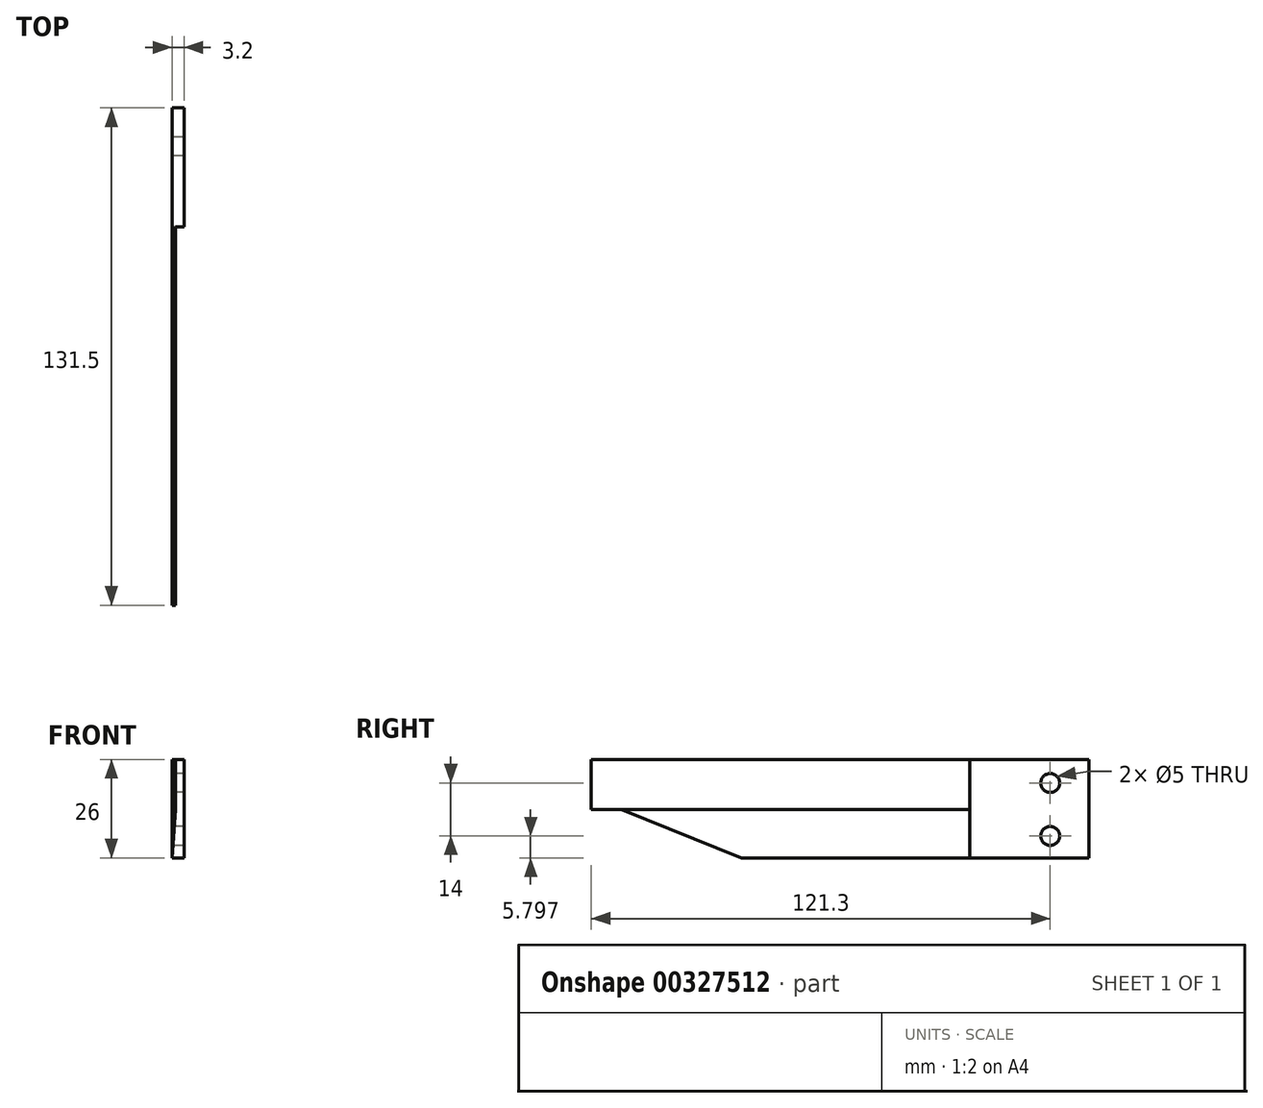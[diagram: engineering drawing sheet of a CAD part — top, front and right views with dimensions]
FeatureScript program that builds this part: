
annotation { "Feature Type Name" : "Feature", "Feature Type Description" : "" }
export const myFeature = defineFeature(function(context is Context, id is Id, definition is map)
    precondition{}
    {
        {
            var Q0;
            Q0=qCreatedBy(makeId("Front.planeOp"),FACE);
            var sketch = newSketch(context, id + "F0", { "sketchPlane" : qUnion([Q0])});
            skLineSegment(sketch, "E0.bottom", {"start": v(-9.66, 11.85) * mm, "end": v(-6.46, 11.85) * mm});
            skLineSegment(sketch, "E0.top", {"start": v(-9.66, -14.15) * mm, "end": v(-6.46, -14.15) * mm});
            skLineSegment(sketch, "E0.left", {"start": v(-9.66, 11.85) * mm, "end": v(-9.66, -14.15) * mm});
            skLineSegment(sketch, "E0.right", {"start": v(-6.46, 11.85) * mm, "end": v(-6.46, -14.15) * mm});
            skLineSegment(sketch, "E1", {"start": v(-6.46, -14.15) * mm, "end": v(-8.66, -14.15) * mm});
            skLineSegment(sketch, "E2", {"start": v(-8.66, -1.35) * mm, "end": v(-8.66, 11.85) * mm});
            skLineSegment(sketch, "E3", {"start": v(-8.66, 11.85) * mm, "end": v(-8.66, -1.35) * mm});
            skLineSegment(sketch, "E4", {"start": v(-9.66, -14.15) * mm, "end": v(-8.66, -1.35) * mm});
            skSolve(sketch);
        }
        {
            var Q0;
            Q0 = qSketchRegion(id + "F0", true);
            extrude(context, id + "F1", {"entities" : qUnion([Q0]), "depth" : 31.5 * mm});
        }
        {
            var Q0;
            {var subQ0=sQuery(id+"F0.wireOp",EDGE,"E0.left");Q0=makeQuery(id+"F0.imprint","IMPRINT",FACE,{"disambiguationData":[TD([[makeQuery(id+"F0.imprint","IMPRINT",EDGE,{"derivedFrom":subQ0}),1.0]])]});}
            extrude(context, id + "F2", {"entities" : qUnion([Q0]), "operationType" : NewBodyOperationType.ADD, "depth" : 131.5 * mm});
        }
        {
            var Q0;
            Q0=makeQuery(id+"F2.opExtrude","CAP_VERTEX",VERTEX,{"disambiguationData":[OSD([sQuery(id+"F0.wireOp",EDGE,"E0.bottom"),sQuery(id+"F0.wireOp",EDGE,"E3")])],"isStart":false});
            var Q1;
            Q1=makeQuery(id+"F2.opExtrude","CAP_VERTEX",VERTEX,{"disambiguationData":[OSD([sQuery(id+"F0.wireOp",EDGE,"E0.bottom"),sQuery(id+"F0.wireOp",EDGE,"E0.left")])],"isStart":false});
            var Q2;
            Q2=makeQuery(id+"F2.opExtrude","CAP_VERTEX",VERTEX,{"disambiguationData":[OSD([sQuery(id+"F0.wireOp",EDGE,"E3"),sQuery(id+"F0.wireOp",EDGE,"E4")])],"isStart":false});
            cPlane(context, id + "F3", {"entities" : qUnion([Q0, Q1, Q2]), "cplaneType" : CPlaneType.THREE_POINT, "offset" : 25 * mm, "width" : 150 * mm, "height" : 150 * mm});
        }
        {
            var Q0;
            Q0=qCreatedBy(id+"F3.planeOp",FACE);
            var sketch = newSketch(context, id + "F4", { "sketchPlane" : qUnion([Q0])});
            skLineSegment(sketch, "E5.0.0", {"start": v(8.66, -1.35) * mm, "end": v(8.66, 11.85) * mm});
            skLineSegment(sketch, "E5.0.1", {"start": v(8.66, 11.85) * mm, "end": v(9.66, 11.85) * mm});
            skLineSegment(sketch, "E5.0.2", {"start": v(9.66, 11.85) * mm, "end": v(9.66, -14.15) * mm});
            skLineSegment(sketch, "E5.0.3", {"start": v(9.66, -14.15) * mm, "end": v(8.66, -1.35) * mm});
            skLineSegment(sketch, "E6.0", {"start": v(9.66, 11.85) * mm, "end": v(6.46, 11.85) * mm});
            skLineSegment(sketch, "E7.0", {"start": v(6.46, 11.85) * mm, "end": v(6.46, -14.15) * mm});
            skLineSegment(sketch, "E8.0", {"start": v(6.46, -14.15) * mm, "end": v(8.66, -14.15) * mm});
            skLineSegment(sketch, "E9.0", {"start": v(9.66, -14.15) * mm, "end": v(6.46, -14.15) * mm});
            skLineSegment(sketch, "E10", {"start": v(9.66, 11.85) * mm, "end": v(9.66, 6.05) * mm});
            skLineSegment(sketch, "E11", {"start": v(9.66, 6.05) * mm, "end": v(8.66, 6.05) * mm});
            skSolve(sketch);
        }
        {
            var Q0;
            Q0=qCreatedBy(makeId("Right.planeOp"),FACE);
            var sketch = newSketch(context, id + "F5", { "sketchPlane" : qUnion([Q0])});
            skLineSegment(sketch, "E12.0", {"start": v(-131.5, 11.85) * mm, "end": v(0, 11.85) * mm});
            skPoint(sketch, "E13.0", {"position": v(-131.5, 6.05) * mm});
            skLineSegment(sketch, "E14.0", {"start": v(-131.5, 11.85) * mm, "end": v(-131.5, -14.15) * mm});
            skLineSegment(sketch, "E15.0", {"start": v(-131.5, -14.15) * mm, "end": v(-31.5, -14.15) * mm});
            skLineSegment(sketch, "E16", {"start": v(-131.5, -1.35) * mm, "end": v(-123.5, -1.35) * mm});
            skLineSegment(sketch, "E17", {"start": v(-131.5, -1.35) * mm, "end": v(-131.5, 6.65) * mm});
            skLineSegment(sketch, "E18", {"start": v(-123.5, -1.35) * mm, "end": v(-131.5, 6.65) * mm});
            skLineSegment(sketch, "E19", {"start": v(-123.5, -14.15) * mm, "end": v(-131.5, -14.15) * mm});
            skLineSegment(sketch, "E20", {"start": v(-31.5, -14.15) * mm, "end": v(-91.82, -14.15) * mm});
            skLineSegment(sketch, "E21", {"start": v(-91.82, -14.15) * mm, "end": v(-123.5, -1.35) * mm});
            skLineSegment(sketch, "E22.0", {"start": v(0, 11.85) * mm, "end": v(0, -1.35) * mm});
            skPoint(sketch, "E23.0", {"position": v(0, -7.75) * mm});
            skLineSegment(sketch, "E24.0", {"start": v(-31.5, 11.85) * mm, "end": v(-31.5, -14.15) * mm});
            skLineSegment(sketch, "E25.0.0", {"start": v(0, -14.15) * mm, "end": v(0, 11.85) * mm});
            skLineSegment(sketch, "E25.0.1", {"start": v(0, 11.85) * mm, "end": v(-31.5, 11.85) * mm});
            skLineSegment(sketch, "E25.0.3", {"start": v(-31.5, -14.15) * mm, "end": v(0, -14.15) * mm});
            skLineSegment(sketch, "E26", {"start": v(0, -1.35) * mm, "end": v(-10.2, -1.35) * mm});
            skLineSegment(sketch, "E27", {"start": v(-10.2, -1.35) * mm, "end": v(-10.2, 5.65) * mm});
            skLineSegment(sketch, "E28", {"start": v(-10.2, -1.35) * mm, "end": v(-10.2, -8.35) * mm});
            skSolve(sketch);
        }
        {
            var Q0;
            {var subQ2=sQuery(id+"F5.wireOp",EDGE,"E16");Q0=makeQuery(id+"F5.imprint","IMPRINT",FACE,{"disambiguationData":[TD([[makeQuery(id+"F5.imprint","IMPRINT",EDGE,{"derivedFrom":subQ2}),-1.0]])]});}
            var Q1;
            Q1=makeQuery(id+"F5.imprint","IMPRINT",FACE,{"disambiguationData":[TD([[makeQuery(id+"F5.imprint","IMPRINT",EDGE,{"derivedFrom":sQuery(id+"F5.wireOp",EDGE,"E17")}),-1.0]])]});
            var Q2;
            Q2=makeQuery(id+"F5.imprint","IMPRINT",FACE,{"disambiguationData":[TD([[makeQuery(id+"F5.imprint","IMPRINT",EDGE,{"derivedFrom":sQuery(id+"F5.wireOp",EDGE,"E15.0")}),1.0]])]});
            extrude(context, id + "F6", {"entities" : qUnion([Q0, Q1, Q2]), "operationType" : NewBodyOperationType.REMOVE, "oppositeDirection" : true, "depth" : 25 * mm});
        }
        {
            var Q0;
            Q0=sQuery(id+"F5.wireOp",VERTEX,"E27.end");
            var Q1;
            Q1=sQuery(id+"F5.wireOp",VERTEX,"E28.end");
            var Q2;
            Q2=makeQuery(id+"F1.opExtrude","SWEPT_BODY",BODY,{"disambiguationData":[OSD([sQuery(id+"F0.wireOp",EDGE,"E0.bottom"),sQuery(id+"F0.wireOp",EDGE,"E0.top"),sQuery(id+"F0.wireOp",EDGE,"E0.left"),sQuery(id+"F0.wireOp",EDGE,"E0.right"),sQuery(id+"F0.wireOp",EDGE,"E1")])]});
            hole(context, id + "F7", {"style" : HoleStyle.SIMPLE, "endStyle" : HoleEndStyle.BLIND, "holeDiameter" : 5 * mm, "holeDepth" : 300 * mm, "tappedDepth" : 12 * mm, "tapClearance" : 3, "locations" : qUnion([Q0, Q1]), "scope" : qUnion([Q2]), "startStyle" : HoleStartStyle.PART});
        }
    });
